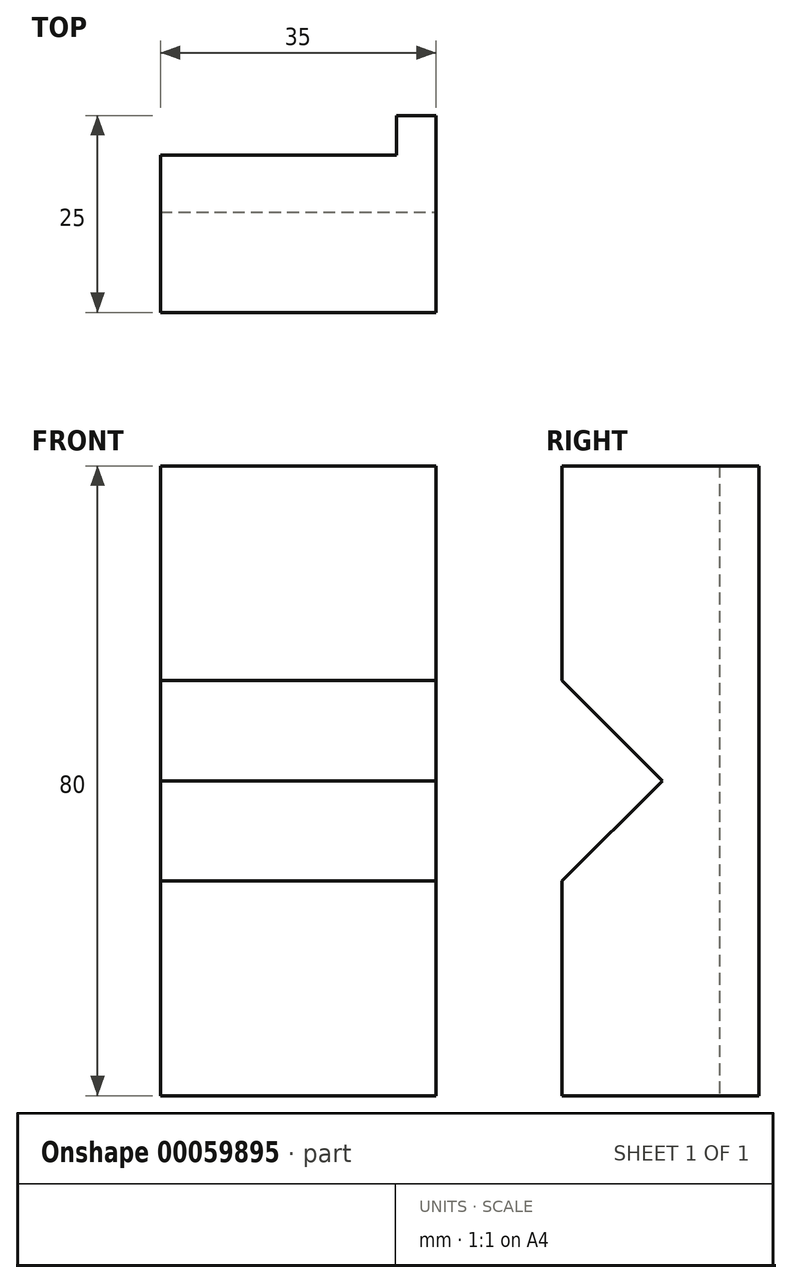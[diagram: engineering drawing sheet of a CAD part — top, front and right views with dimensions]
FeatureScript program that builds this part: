
annotation { "Feature Type Name" : "Feature", "Feature Type Description" : "" }
export const myFeature = defineFeature(function(context is Context, id is Id, definition is map)
    precondition{}
    {
        {
            var Q0;
            Q0=qCreatedBy(makeId("Top.planeOp"),FACE);
            var sketch = newSketch(context, id + "F0", { "sketchPlane" : qUnion([Q0])});
            skLineSegment(sketch, "E0.rect.bottom", {"start": v(12.5, 12.5) * mm, "end": v(17.5, 12.5) * mm});
            skLineSegment(sketch, "E0.rect.top", {"start": v(-17.5, -12.5) * mm, "end": v(17.5, -12.5) * mm});
            skLineSegment(sketch, "E0.rect.left", {"start": v(-17.5, 7.5) * mm, "end": v(-17.5, -12.5) * mm});
            skLineSegment(sketch, "E0.rect.right", {"start": v(17.5, 12.5) * mm, "end": v(17.5, -12.5) * mm});
            skPoint(sketch, "E0.rect.middle", {"position": v(0, 0) * mm});
            skLineSegment(sketch, "E1.top", {"start": v(-17.5, 7.5) * mm, "end": v(12.5, 7.5) * mm});
            skLineSegment(sketch, "E1.right", {"start": v(12.5, 12.5) * mm, "end": v(12.5, 7.5) * mm});
            skPoint(sketch, "E2.orphan", {"position": v(-17.5, 12.5) * mm});
            skSolve(sketch);
        }
        {
            var Q0;
            Q0=makeQuery(id+"F0.imprint","IMPRINT",FACE,{"disambiguationData":[TD([[makeQuery(id+"F0.imprint","IMPRINT",EDGE,{"derivedFrom":sQuery(id+"F0.wireOp",EDGE,"E0.rect.bottom")}),-1.0]])]});
            extrude(context, id + "F1", {"entities" : qUnion([Q0]), "depth" : 80 * mm});
        }
        {
            var Q0;
            Q0=makeQuery(id+"F1.opExtrude","SWEPT_FACE",FACE,{"disambiguationData":[OSD([sQuery(id+"F0.wireOp",EDGE,"E0.rect.right")])]});
            var sketch = newSketch(context, id + "F2", { "sketchPlane" : qUnion([Q0])});
            skLineSegment(sketch, "E3", {"start": v(-12.5, 40) * mm, "end": v(0.24, 40) * mm, "construction": true});
            skLineSegment(sketch, "E4", {"start": v(-12.5, 40) * mm, "end": v(-12.5, 52.74) * mm, "construction": true});
            skLineSegment(sketch, "E5", {"start": v(-12.5, 40) * mm, "end": v(-12.5, 27.26) * mm, "construction": true});
            skLineSegment(sketch, "E6", {"start": v(-12.5, 52.74) * mm, "end": v(0.24, 40) * mm});
            skLineSegment(sketch, "E7", {"start": v(-12.5, 27.26) * mm, "end": v(0.24, 40) * mm});
            skLineSegment(sketch, "E8", {"start": v(-12.5, 27.26) * mm, "end": v(-12.5, 52.74) * mm});
            skSolve(sketch);
        }
        {
            var Q0;
            Q0=makeQuery(id+"F2.imprint","IMPRINT",FACE,{"disambiguationData":[TD([[makeQuery(id+"F2.imprint","IMPRINT",EDGE,{"derivedFrom":sQuery(id+"F2.wireOp",EDGE,"E6")}),-1.0]])]});
            extrude(context, id + "F3", {"entities" : qUnion([Q0]), "operationType" : NewBodyOperationType.REMOVE, "endBound" : BoundingType.THROUGH_ALL, "oppositeDirection" : true, "depth" : 25 * mm});
        }
    });
